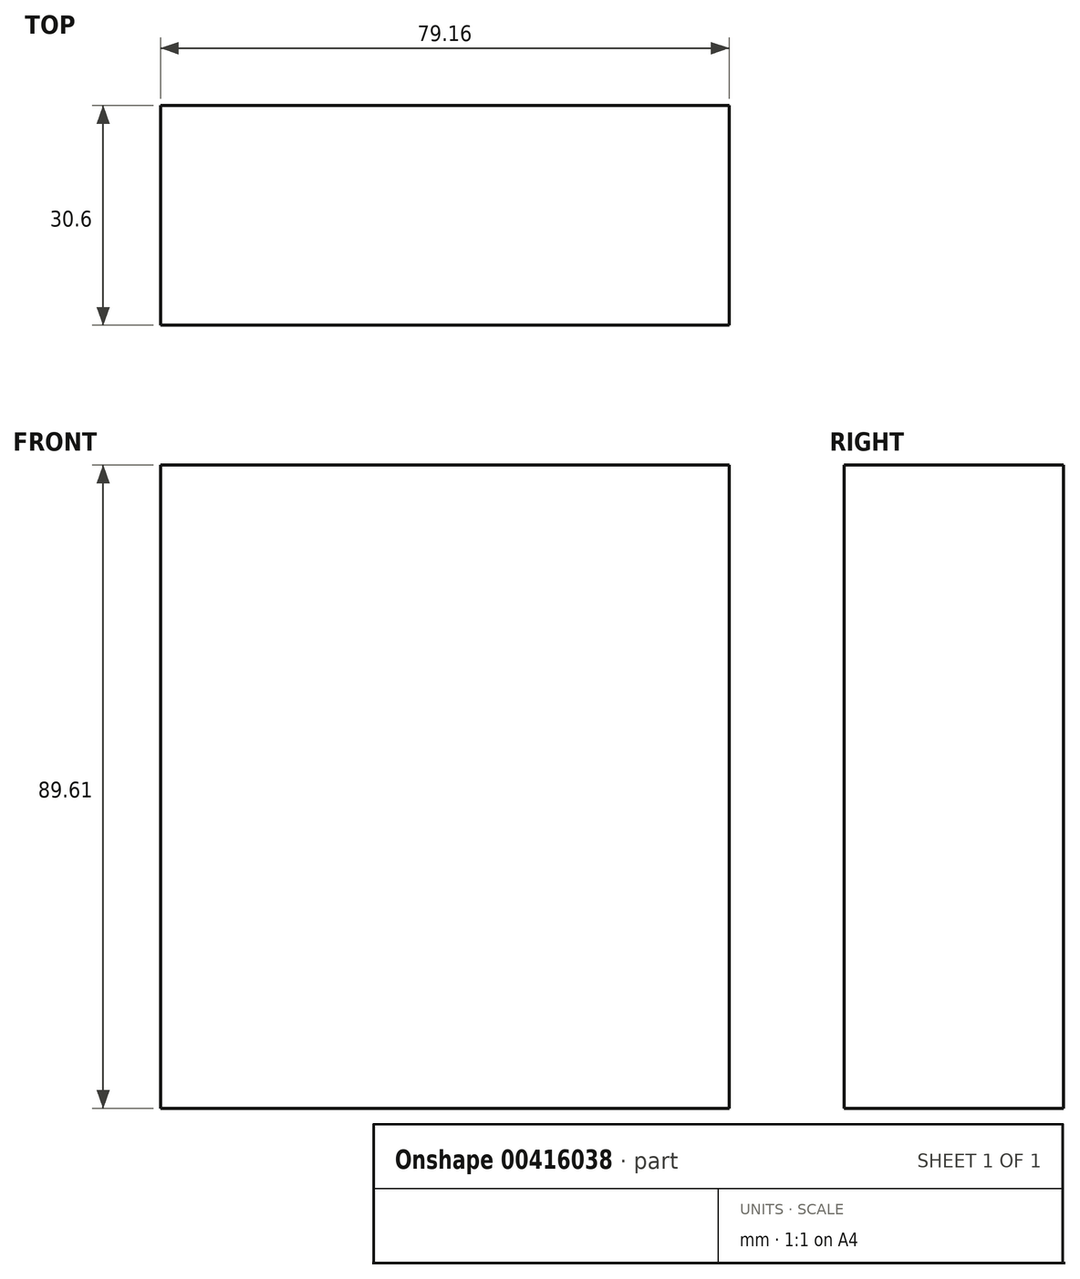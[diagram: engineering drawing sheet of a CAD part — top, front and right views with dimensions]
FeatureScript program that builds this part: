
annotation { "Feature Type Name" : "Feature", "Feature Type Description" : "" }
export const myFeature = defineFeature(function(context is Context, id is Id, definition is map)
    precondition{}
    {
        {
            var Q0;
            Q0=qCreatedBy(makeId("Front.planeOp"),FACE);
            var sketch = newSketch(context, id + "F0", { "sketchPlane" : qUnion([Q0])});
            skLineSegment(sketch, "E0.bottom", {"start": v(-42.97, 41.13) * mm, "end": v(36.19, 41.13) * mm});
            skLineSegment(sketch, "E0.top", {"start": v(-42.97, -48.48) * mm, "end": v(36.19, -48.48) * mm});
            skLineSegment(sketch, "E0.left", {"start": v(-42.97, 41.13) * mm, "end": v(-42.97, -48.48) * mm});
            skLineSegment(sketch, "E0.right", {"start": v(36.19, 41.13) * mm, "end": v(36.19, -48.48) * mm});
            skSolve(sketch);
        }
        {
            var Q0;
            Q0 = qSketchRegion(id + "F0", true);
            extrude(context, id + "F1", {"entities" : qUnion([Q0]), "depth" : 30.6 * mm});
        }
    });
